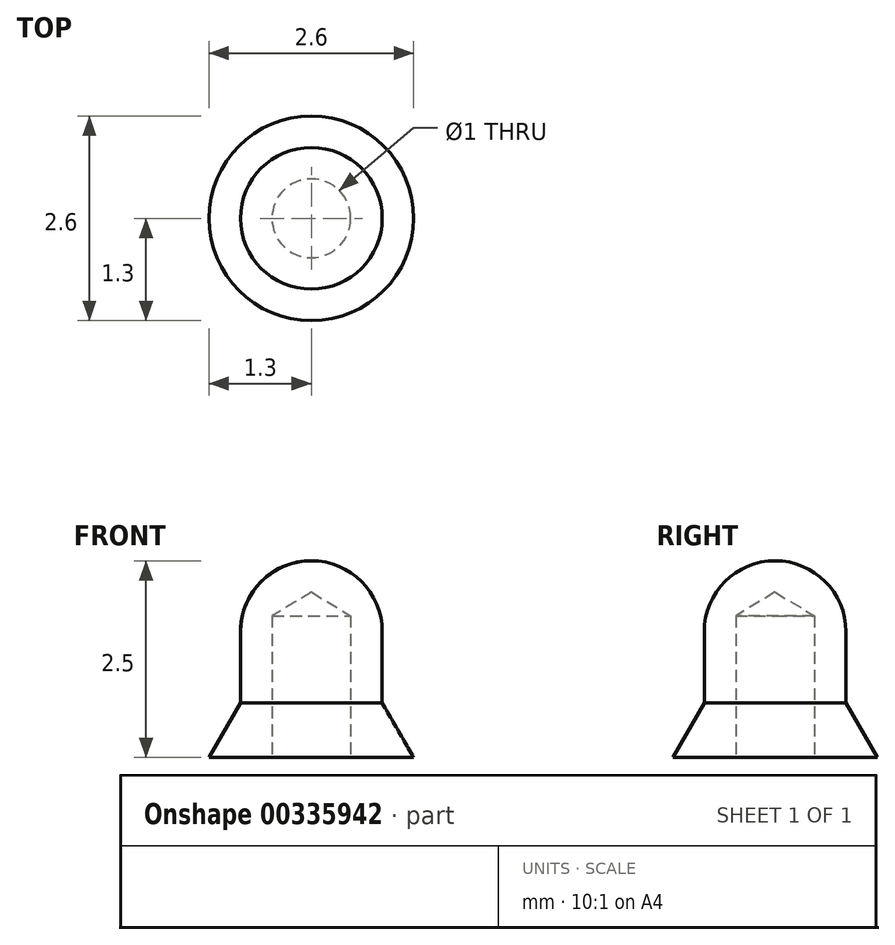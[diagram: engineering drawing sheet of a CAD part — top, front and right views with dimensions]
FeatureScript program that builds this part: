
annotation { "Feature Type Name" : "Feature", "Feature Type Description" : "" }
export const myFeature = defineFeature(function(context is Context, id is Id, definition is map)
    precondition{}
    {
        {
            var Q0;
            Q0=qCreatedBy(makeId("Front.planeOp"),FACE);
            var sketch = newSketch(context, id + "F0", { "sketchPlane" : qUnion([Q0])});
            skLineSegment(sketch, "E0", {"start": v(0, 0) * mm, "end": v(-1.3, 0) * mm});
            skLineSegment(sketch, "E1", {"start": v(-1.3, 0) * mm, "end": v(-0.9, 0.7) * mm});
            skLineSegment(sketch, "E2", {"start": v(-0.9, 0.7) * mm, "end": v(-0.9, 1.6) * mm});
            skArc(sketch, "E3", {"start": v(-0.9, 1.6) * mm, "mid": v(-0.64, 2.24) * mm, "end": v(0, 2.5) * mm});
            skLineSegment(sketch, "E4", {"start": v(0, 2.5) * mm, "end": v(0, 0) * mm});
            skSolve(sketch);
        }
        {
            var Q0;
            Q0 = qSketchRegion(id + "F0", true);
            var Q1;
            Q1=sQuery(id+"F0.wireOp",EDGE,"E4");
            revolve(context, id + "F1", {"entities" : qUnion([Q0]), "axis" : qUnion([Q1]), "revolveType" : RevolveType.FULL});
        }
        {
            var Q0;
            Q0=makeQuery(id+"F1.opRevolve","SWEPT_FACE",FACE,{"disambiguationData":[OSD([sQuery(id+"F0.wireOp",EDGE,"E0")])]});
            var sketch = newSketch(context, id + "F2", { "sketchPlane" : qUnion([Q0])});
            skPoint(sketch, "E5", {"position": v(0, 0) * mm});
            skSolve(sketch);
        }
        {
            var Q0;
            Q0=sQuery(id+"F2.wireOp",VERTEX,"E5");
            var Q1;
            Q1=makeQuery(id+"F1.opRevolve","SWEPT_BODY",BODY,{"disambiguationData":[OSD([sQuery(id+"F0.wireOp",EDGE,"E0"),sQuery(id+"F0.wireOp",EDGE,"E1"),sQuery(id+"F0.wireOp",EDGE,"E2"),sQuery(id+"F0.wireOp",EDGE,"E3"),sQuery(id+"F0.wireOp",EDGE,"E4")])]});
            hole(context, id + "F3", {"style" : HoleStyle.SIMPLE, "endStyle" : HoleEndStyle.BLIND, "holeDiameter" : 1 * mm, "holeDepth" : 1.8 * mm, "tappedDepth" : 12 * mm, "tapClearance" : 3, "locations" : qUnion([Q0]), "scope" : qUnion([Q1])});
        }
    });
